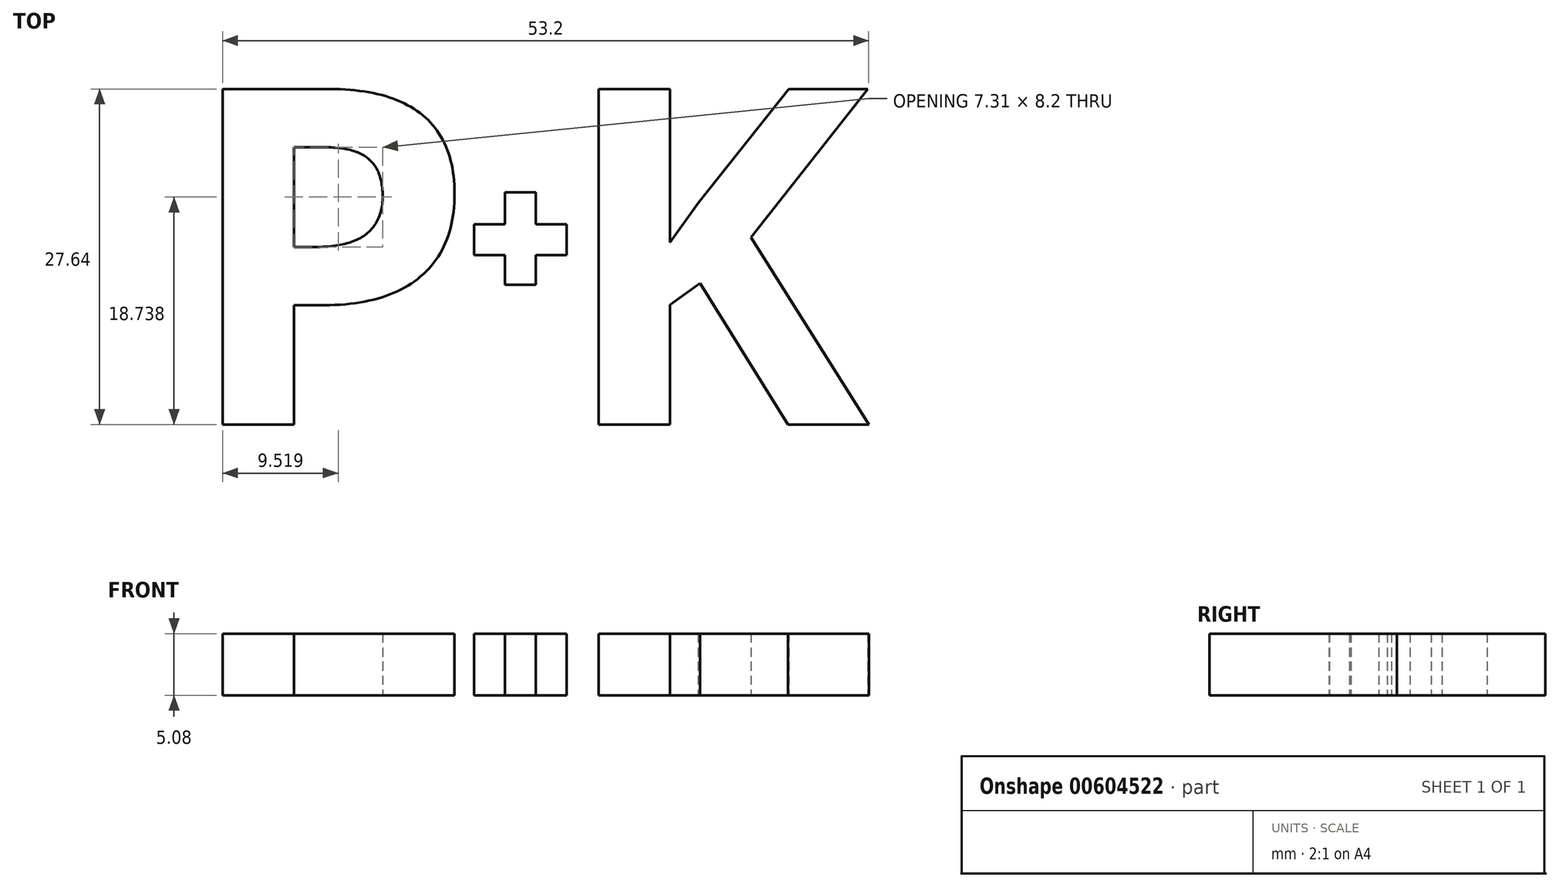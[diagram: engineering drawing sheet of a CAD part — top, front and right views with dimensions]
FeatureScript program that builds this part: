
annotation { "Feature Type Name" : "Feature", "Feature Type Description" : "" }
export const myFeature = defineFeature(function(context is Context, id is Id, definition is map)
    precondition{}
    {
        {
            var Q0;
            Q0=qCreatedBy(makeId("Top.planeOp"),FACE);
            var sketch = newSketch(context, id + "F0", { "sketchPlane" : qUnion([Q0])});
            skLineSegment(sketch, "E0.bottom", {"start": v(-1.27, 3.9) * mm, "end": v(1.27, 3.9) * mm});
            skLineSegment(sketch, "E0.top", {"start": v(-1.27, -3.73) * mm, "end": v(1.27, -3.73) * mm});
            skLineSegment(sketch, "E0.left", {"start": v(-1.27, 3.9) * mm, "end": v(-1.27, -3.73) * mm});
            skLineSegment(sketch, "E0.right", {"start": v(1.27, 3.9) * mm, "end": v(1.27, -3.73) * mm});
            skLineSegment(sketch, "E1.bottom", {"start": v(-3.8, 1.26) * mm, "end": v(3.81, 1.26) * mm});
            skLineSegment(sketch, "E1.top", {"start": v(-3.8, -1.28) * mm, "end": v(3.81, -1.28) * mm});
            skLineSegment(sketch, "E1.left", {"start": v(-3.8, 1.26) * mm, "end": v(-3.8, -1.28) * mm});
            skLineSegment(sketch, "E1.right", {"start": v(3.81, 1.26) * mm, "end": v(3.81, -1.28) * mm});
            skSolve(sketch);
        }
        {
            var Q0;
            {var subQ5=sQuery(id+"F0.wireOp",EDGE,"E1.left");Q0=makeQuery(id+"F0.imprint","IMPRINT",FACE,{"disambiguationData":[TD([[makeQuery(id+"F0.imprint","IMPRINT",EDGE,{"derivedFrom":subQ5}),1.0]])]});}
            var Q1;
            {var subQ0=sQuery(id+"F0.wireOp",EDGE,"E1.bottom");var subQ1=sQuery(id+"F0.wireOp",EDGE,"E0.left");var subQ2=makeQuery(id+"F0.imprint","INTERSECT",VERTEX,{"derivedFrom":[subQ1,subQ0]});Q1=makeQuery(id+"F0.imprint","IMPRINT",FACE,{"disambiguationData":[TD([[makeQuery(id+"F0.imprint","IMPRINT",EDGE,{"disambiguationData":[TD([[subQ2,-1.0]])],"derivedFrom":subQ1}),1.0]])]});}
            var Q2;
            {var subQ0=sQuery(id+"F0.wireOp",EDGE,"E0.bottom");Q2=makeQuery(id+"F0.imprint","IMPRINT",FACE,{"disambiguationData":[TD([[makeQuery(id+"F0.imprint","IMPRINT",EDGE,{"derivedFrom":subQ0}),-1.0]])]});}
            var Q3;
            {var subQ5=sQuery(id+"F0.wireOp",EDGE,"E1.right");Q3=makeQuery(id+"F0.imprint","IMPRINT",FACE,{"disambiguationData":[TD([[makeQuery(id+"F0.imprint","IMPRINT",EDGE,{"derivedFrom":subQ5}),-1.0]])]});}
            var Q4;
            {var subQ0=sQuery(id+"F0.wireOp",EDGE,"E0.top");Q4=makeQuery(id+"F0.imprint","IMPRINT",FACE,{"disambiguationData":[TD([[makeQuery(id+"F0.imprint","IMPRINT",EDGE,{"derivedFrom":subQ0}),1.0]])]});}
            var Q5;
            Q5=sQuery(id+"F0.wireOp",EDGE,"E1.bottom");
            var Q6;
            Q6=sQuery(id+"F0.wireOp",EDGE,"E1.top");
            var Q7;
            Q7=sQuery(id+"F0.wireOp",EDGE,"E0.left");
            var Q8;
            Q8=sQuery(id+"F0.wireOp",EDGE,"E0.right");
            var Q9;
            Q9=sQuery(id+"F0.wireOp",EDGE,"E1.right");
            var Q10;
            Q10=sQuery(id+"F0.wireOp",EDGE,"E0.bottom");
            var Q11;
            Q11=sQuery(id+"F0.wireOp",EDGE,"E1.left");
            var Q12;
            Q12=sQuery(id+"F0.wireOp",EDGE,"E0.top");
            extrude(context, id + "F1", {"entities" : qUnion([Q0, Q1, Q2, Q3, Q4]), "surfaceEntities" : qUnion([Q5, Q6, Q7, Q8, Q9, Q10, Q11, Q12]), "depth" : 5.08 * mm, "offsetDistance" : 25.4 * mm});
        }
        {
            var Q0;
            Q0=qCreatedBy(makeId("Top.planeOp"),FACE);
            var sketch = newSketch(context, id + "F2", { "sketchPlane" : qUnion([Q0])});
            skText(sketch, "E2", { "text": "P", "fontName": "OpenSans-Bold.ttf"});
            skText(sketch, "E3", { "text": "K", "fontName": "OpenSans-Bold.ttf"});
            const initialGuessF2  = {"E2": [-0.02798, -0.01523, 1, 0, 0.02788], "E3": [0.00299, -0.01523, 1, 0, 0.02788]};
            skSetInitialGuess(sketch, initialGuessF2);
            skSolve(sketch);
        }
        {
            var Q0;
            Q0=makeQuery(id+"F2.imprint","IMPRINT",FACE,{"disambiguationData":[TD([[makeQuery(id+"F2.imprint","IMPRINT",EDGE,{"derivedFrom":sQuery(id+"F2.wireOp",EDGE,"E2.sketch_text.stroke-0")}),-1.0]])]});
            var Q1;
            Q1=makeQuery(id+"F2.imprint","IMPRINT",FACE,{"disambiguationData":[TD([[makeQuery(id+"F2.imprint","IMPRINT",EDGE,{"derivedFrom":sQuery(id+"F2.wireOp",EDGE,"E3.sketch_text.stroke-0")}),-1.0]])]});
            extrude(context, id + "F3", {"entities" : qUnion([Q0, Q1]), "depth" : 5.08 * mm, "offsetDistance" : 25.4 * mm});
        }
    });
